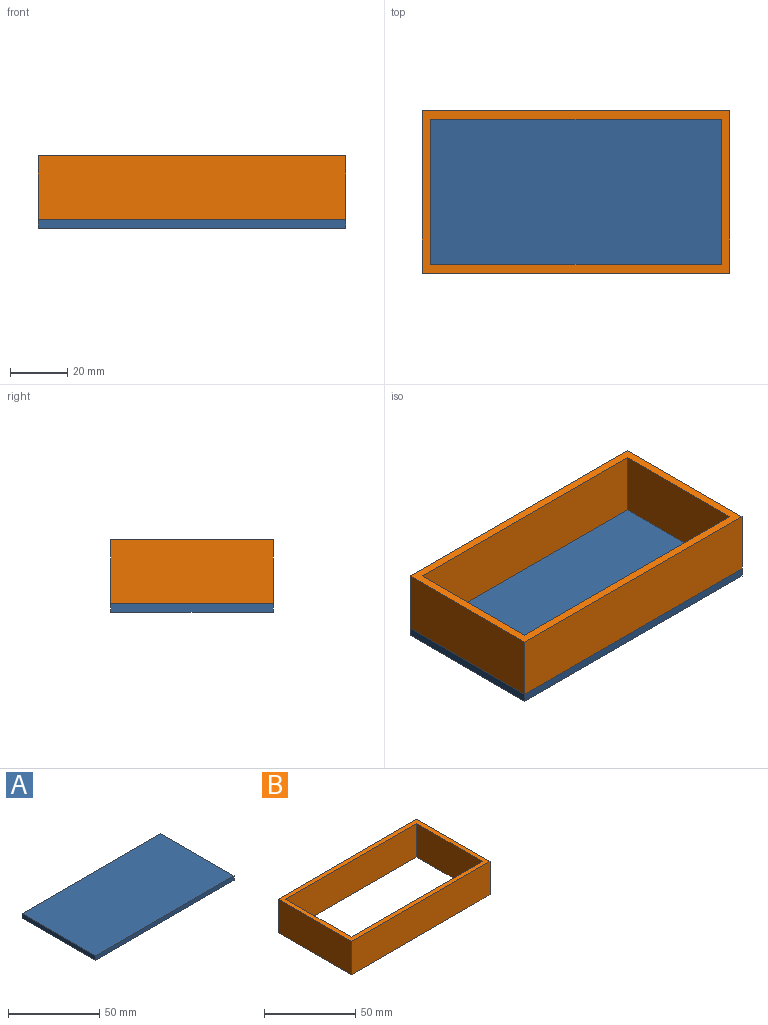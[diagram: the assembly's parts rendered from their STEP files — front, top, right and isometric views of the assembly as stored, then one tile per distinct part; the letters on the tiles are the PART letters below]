
ASSEMBLY  parts=2 mates=1
PART A: 6 faces, bbox 107.6x56.8x3 mm
  f0: plane 107.6x3mm, normal (0,1,0), area 322.8mm2, adj f1,f3,f4,f5
  f1: plane 56.8x3mm, normal (-1,0,0), area 170.4mm2, adj f0,f2,f4,f5
  f2: plane 107.6x3mm, normal (0,-1,0), area 322.8mm2, adj f1,f3,f4,f5
  f3: plane 56.8x3mm, normal (1,0,0), area 170.4mm2, adj f0,f2,f4,f5
  f4: plane 107.6x56.8mm, normal (0,0,1), area 6111.7mm2, adj f0,f1,f2,f3
  f5: plane 107.6x56.8mm, normal (0,0,-1), area 6111.7mm2, adj f0,f1,f2,f3
PART B: 10 faces, bbox 107.6x56.8x22.4 mm
  f0: plane 107.6x22.4mm, normal (0,1,0), area 2410.2mm2, adj f1,f7,f8,f9
  f1: plane 56.8x22.4mm, normal (-1,0,0), area 1272.3mm2, adj f0,f2,f8,f9
  f2: plane 107.6x22.4mm, normal (0,-1,0), area 2410.2mm2, adj f1,f7,f8,f9
  f3: plane 101.6x22.4mm, normal (0,1,0), area 2275.8mm2, adj f4,f6,f8,f9
  f4: plane 50.8x22.4mm, normal (1,0,0), area 1137.9mm2, adj f3,f5,f8,f9
  f5: plane 101.6x22.4mm, normal (0,-1,0), area 2275.8mm2, adj f4,f6,f8,f9
  f6: plane 50.8x22.4mm, normal (-1,0,0), area 1137.9mm2, adj f3,f5,f8,f9
  f7: plane 56.8x22.4mm, normal (1,0,0), area 1272.3mm2, adj f0,f2,f8,f9
  f8: plane 107.6x56.8mm, normal (0,0,1), area 950.4mm2, adj f0,f1,f2,f3,f4,f5,f6,f7
  f9: plane 107.6x56.8mm, normal (0,0,-1), area 950.4mm2, adj f0,f1,f2,f3,f4,f5,f6,f7
PLACE A t=(-20.68,-1.75,-0.42)mm
PLACE B t=(-20.68,-1.75,2.58)mm
MATE fastened A.f2 <-> B.f2  axis (0,-1,0) through (33.12,-30.15,2.58)mm
